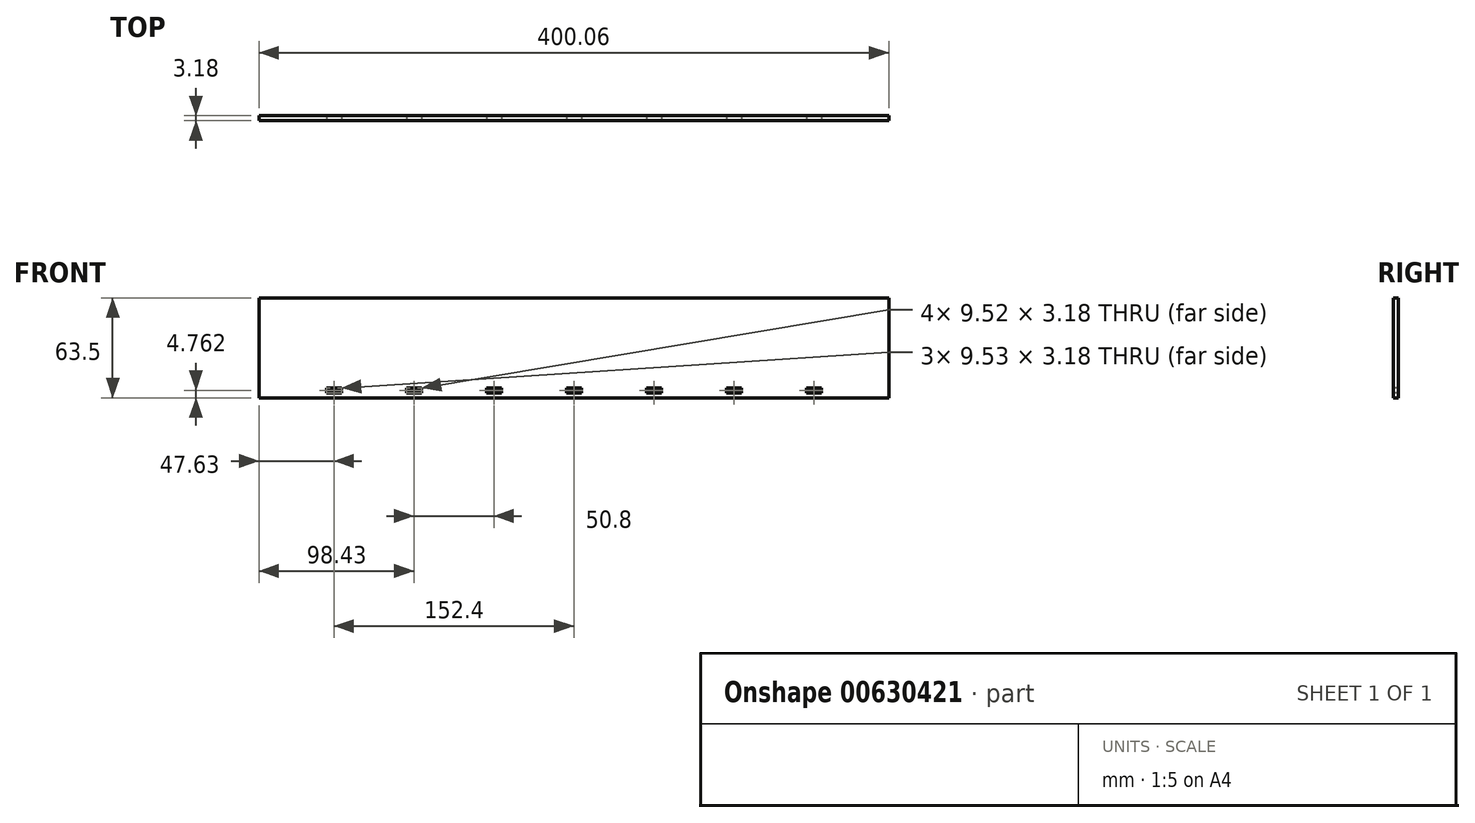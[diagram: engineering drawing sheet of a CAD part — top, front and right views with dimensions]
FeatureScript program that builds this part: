
annotation { "Feature Type Name" : "Feature", "Feature Type Description" : "" }
export const myFeature = defineFeature(function(context is Context, id is Id, definition is map)
    precondition{}
    {
        {
            var Q0;
            Q0=qCreatedBy(makeId("Front.planeOp"),FACE);
            var sketch = newSketch(context, id + "F0", { "sketchPlane" : qUnion([Q0])});
            skLineSegment(sketch, "E0.bottom", {"start": v(200.03, 31.75) * mm, "end": v(-200.02, 31.75) * mm});
            skLineSegment(sketch, "E0.top", {"start": v(200.02, -31.75) * mm, "end": v(-200.03, -31.75) * mm});
            skLineSegment(sketch, "E0.left", {"start": v(200.03, 31.75) * mm, "end": v(200.02, -31.75) * mm});
            skLineSegment(sketch, "E0.right", {"start": v(-200.02, 31.75) * mm, "end": v(-200.03, -31.75) * mm});
            skPoint(sketch, "E0.middle", {"position": v(0, 0) * mm});
            skSolve(sketch);
        }
        {
            var Q0;
            Q0=makeQuery(id+"F0.imprint","IMPRINT",FACE,{"disambiguationData":[TD([[makeQuery(id+"F0.imprint","IMPRINT",EDGE,{"derivedFrom":sQuery(id+"F0.wireOp",EDGE,"E0.bottom")}),1.0]])]});
            extrude(context, id + "F1", {"entities" : qUnion([Q0]), "depth" : 3.17 * mm, "offsetDistance" : 25.4 * mm});
        }
        {
            var Q0;
            Q0=makeQuery(id+"F1.opExtrude","CAP_FACE",FACE,{"disambiguationData":[OSD([sQuery(id+"F0.wireOp",EDGE,"E0.bottom"),sQuery(id+"F0.wireOp",EDGE,"E0.top"),sQuery(id+"F0.wireOp",EDGE,"E0.left"),sQuery(id+"F0.wireOp",EDGE,"E0.right")])],"isStart":false});
            var sketch = newSketch(context, id + "F2", { "sketchPlane" : qUnion([Q0])});
            skLineSegment(sketch, "E1", {"start": v(200.02, -28.58) * mm, "end": v(-200.03, -28.58) * mm, "construction": true});
            skLineSegment(sketch, "E2.bottom", {"start": v(157.16, -28.58) * mm, "end": v(147.64, -28.58) * mm});
            skLineSegment(sketch, "E2.top", {"start": v(157.16, -25.4) * mm, "end": v(147.64, -25.4) * mm});
            skLineSegment(sketch, "E2.left", {"start": v(157.16, -28.58) * mm, "end": v(157.16, -25.4) * mm});
            skLineSegment(sketch, "E2.right", {"start": v(147.64, -28.58) * mm, "end": v(147.64, -25.4) * mm});
            skLineSegment(sketch, "E3.bottom", {"start": v(106.36, -28.58) * mm, "end": v(96.84, -28.58) * mm});
            skLineSegment(sketch, "E3.top", {"start": v(106.36, -25.4) * mm, "end": v(96.84, -25.4) * mm});
            skLineSegment(sketch, "E3.left", {"start": v(106.36, -28.58) * mm, "end": v(106.36, -25.4) * mm});
            skLineSegment(sketch, "E3.right", {"start": v(96.84, -28.58) * mm, "end": v(96.84, -25.4) * mm});
            skLineSegment(sketch, "E4.bottom", {"start": v(55.56, -28.58) * mm, "end": v(46.04, -28.58) * mm});
            skLineSegment(sketch, "E4.top", {"start": v(55.56, -25.4) * mm, "end": v(46.04, -25.4) * mm});
            skLineSegment(sketch, "E4.left", {"start": v(55.56, -28.58) * mm, "end": v(55.56, -25.4) * mm});
            skLineSegment(sketch, "E4.right", {"start": v(46.04, -28.58) * mm, "end": v(46.04, -25.4) * mm});
            skPoint(sketch, "E5", {"position": v(152.4, -25.4) * mm});
            skPoint(sketch, "E6", {"position": v(101.6, -25.4) * mm});
            skPoint(sketch, "E7", {"position": v(50.8, -25.4) * mm});
            skLineSegment(sketch, "E8.MirrorCS", {"start": v(-106.36, -25.4) * mm, "end": v(-96.84, -25.4) * mm});
            skLineSegment(sketch, "E9.MirrorCS", {"start": v(-106.36, -28.58) * mm, "end": v(-106.36, -25.4) * mm});
            skLineSegment(sketch, "E10.MirrorCS", {"start": v(-96.84, -28.58) * mm, "end": v(-96.84, -25.4) * mm});
            skLineSegment(sketch, "E11.MirrorCS", {"start": v(-55.56, -28.58) * mm, "end": v(-46.04, -28.58) * mm});
            skLineSegment(sketch, "E12.MirrorCS", {"start": v(-55.56, -25.4) * mm, "end": v(-46.04, -25.4) * mm});
            skLineSegment(sketch, "E13.MirrorCS", {"start": v(-55.56, -28.58) * mm, "end": v(-55.56, -25.4) * mm});
            skLineSegment(sketch, "E14.MirrorCS", {"start": v(-46.04, -28.58) * mm, "end": v(-46.04, -25.4) * mm});
            skLineSegment(sketch, "E15.MirrorCS", {"start": v(-157.16, -28.58) * mm, "end": v(-147.64, -28.58) * mm});
            skLineSegment(sketch, "E16.MirrorCS", {"start": v(-157.16, -25.4) * mm, "end": v(-147.64, -25.4) * mm});
            skLineSegment(sketch, "E17.MirrorCS", {"start": v(-157.16, -28.58) * mm, "end": v(-157.16, -25.4) * mm});
            skPoint(sketch, "E18.MirrorP", {"position": v(-50.8, -25.4) * mm});
            skLineSegment(sketch, "E19.MirrorCS", {"start": v(-106.36, -28.58) * mm, "end": v(-96.84, -28.58) * mm});
            skPoint(sketch, "E20.MirrorP", {"position": v(-101.6, -25.4) * mm});
            skPoint(sketch, "E21.MirrorP", {"position": v(-152.4, -25.4) * mm});
            skLineSegment(sketch, "E22.MirrorCS", {"start": v(-147.64, -28.58) * mm, "end": v(-147.64, -25.4) * mm});
            skLineSegment(sketch, "E23.bottom", {"start": v(4.76, -28.58) * mm, "end": v(-4.76, -28.58) * mm});
            skLineSegment(sketch, "E23.top", {"start": v(4.76, -25.4) * mm, "end": v(-4.76, -25.4) * mm});
            skLineSegment(sketch, "E23.left", {"start": v(4.76, -28.58) * mm, "end": v(4.76, -25.4) * mm});
            skLineSegment(sketch, "E23.right", {"start": v(-4.76, -28.58) * mm, "end": v(-4.76, -25.4) * mm});
            skPoint(sketch, "E24", {"position": v(0, -25.4) * mm});
            skSolve(sketch);
        }
        {
            var Q0;
            Q0 = qSketchRegion(id + "F2", true);
            extrude(context, id + "F3", {"entities" : qUnion([Q0]), "operationType" : NewBodyOperationType.REMOVE, "oppositeDirection" : true, "depth" : 25.4 * mm, "offsetDistance" : 25.4 * mm});
        }
    });
